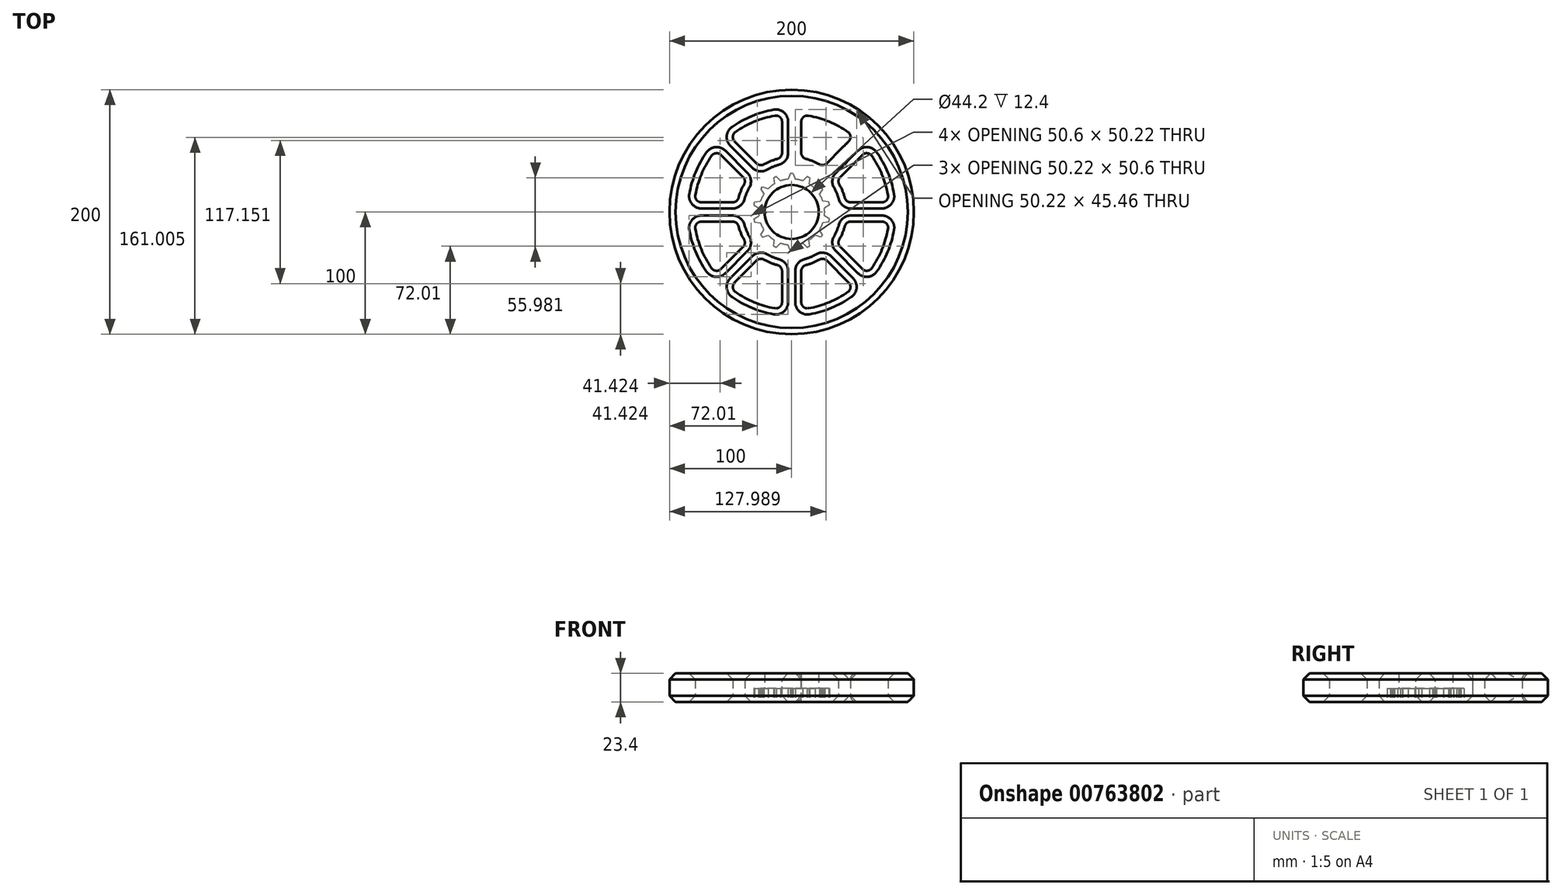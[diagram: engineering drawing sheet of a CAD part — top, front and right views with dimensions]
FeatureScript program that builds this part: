
annotation { "Feature Type Name" : "Feature", "Feature Type Description" : "" }
export const myFeature = defineFeature(function(context is Context, id is Id, definition is map)
    precondition{}
    {
        {
            var Q0;
            Q0=qCreatedBy(makeId("Top.planeOp"),FACE);
            var sketch = newSketch(context, id + "F0", { "sketchPlane" : qUnion([Q0])});
            skCircle(sketch, "E0", {"center": v(0, 0) * mm, "radius": 22.1 * mm});
            skCircle(sketch, "E1", {"center": v(0, 0) * mm, "radius": 100 * mm});
            skSolve(sketch);
        }
        {
            var Q0;
            Q0 = qSketchRegion(id + "F0", true);
            extrude(context, id + "F1", {"entities" : qUnion([Q0]), "depth" : 23.4 * mm, "offsetDistance" : 25 * mm});
        }
        {
            var Q0;
            Q0=makeQuery(id+"F1.opExtrude","CAP_FACE",FACE,{"disambiguationData":[OSD([sQuery(id+"F0.wireOp",EDGE,"E0"),sQuery(id+"F0.wireOp",EDGE,"E1")])],"isStart":true});
            var sketch = newSketch(context, id + "F2", { "sketchPlane" : qUnion([Q0])});
            skCircle(sketch, "E2.0", {"center": v(0, 0) * mm, "radius": 22.1 * mm});
            skArc(sketch, "E3", {"start": v(2.9, -26.84) * mm, "mid": v(6, -26.32) * mm, "end": v(9.03, -25.44) * mm});
            skLineSegment(sketch, "E4", {"start": v(0, 0) * mm, "end": v(0, 59.3) * mm, "construction": true});
            skArc(sketch, "E5", {"start": v(0, -31.5) * mm, "mid": v(0.63, -31.5) * mm, "end": v(1.25, -31.48) * mm, "construction": true});
            skLineSegment(sketch, "E6", {"start": v(0, 31.5) * mm, "end": v(-1.25, 31.48) * mm});
            skLineSegment(sketch, "E7.MirrorCS", {"start": v(0, 31.5) * mm, "end": v(1.25, 31.48) * mm});
            skLineSegment(sketch, "E8", {"start": v(-1.25, 31.48) * mm, "end": v(-2.9, 26.84) * mm});
            skLineSegment(sketch, "E9", {"start": v(1.25, 31.48) * mm, "end": v(2.9, 26.84) * mm});
            skArc(sketch, "E10.1.0", {"start": v(0, -31.5) * mm, "mid": v(0.63, -31.5) * mm, "end": v(1.25, -31.48) * mm});
            skLineSegment(sketch, "E11.1.0", {"start": v(-12.53, 28.9) * mm, "end": v(-9.03, 25.44) * mm});
            skLineSegment(sketch, "E11.1.1", {"start": v(-14.78, 27.82) * mm, "end": v(-14.26, 22.93) * mm});
            skLineSegment(sketch, "E11.1.2", {"start": v(-13.67, 28.38) * mm, "end": v(-12.53, 28.9) * mm});
            skLineSegment(sketch, "E11.1.3", {"start": v(-13.67, 28.38) * mm, "end": v(-14.78, 27.82) * mm});
            skLineSegment(sketch, "E11.2.0", {"start": v(-23.83, 20.6) * mm, "end": v(-19.18, 19) * mm});
            skLineSegment(sketch, "E11.2.1", {"start": v(-25.39, 18.65) * mm, "end": v(-22.8, 14.47) * mm});
            skLineSegment(sketch, "E11.2.2", {"start": v(-24.63, 19.64) * mm, "end": v(-23.83, 20.6) * mm});
            skLineSegment(sketch, "E11.2.3", {"start": v(-24.63, 19.64) * mm, "end": v(-25.39, 18.65) * mm});
            skLineSegment(sketch, "E11.3.0", {"start": v(-30.4, 8.22) * mm, "end": v(-25.53, 8.8) * mm});
            skLineSegment(sketch, "E11.3.1", {"start": v(-30.96, 5.79) * mm, "end": v(-26.82, 3.15) * mm});
            skLineSegment(sketch, "E11.3.2", {"start": v(-30.71, 7) * mm, "end": v(-30.4, 8.22) * mm});
            skLineSegment(sketch, "E11.3.3", {"start": v(-30.71, 7) * mm, "end": v(-30.96, 5.79) * mm});
            skLineSegment(sketch, "E11.4.0", {"start": v(-30.96, -5.79) * mm, "end": v(-26.82, -3.15) * mm});
            skLineSegment(sketch, "E11.4.1", {"start": v(-30.4, -8.22) * mm, "end": v(-25.53, -8.8) * mm});
            skLineSegment(sketch, "E11.4.2", {"start": v(-30.71, -7) * mm, "end": v(-30.96, -5.79) * mm});
            skLineSegment(sketch, "E11.4.3", {"start": v(-30.71, -7) * mm, "end": v(-30.4, -8.22) * mm});
            skLineSegment(sketch, "E11.5.0", {"start": v(-25.39, -18.65) * mm, "end": v(-22.8, -14.47) * mm});
            skLineSegment(sketch, "E11.5.1", {"start": v(-23.83, -20.6) * mm, "end": v(-19.18, -19) * mm});
            skLineSegment(sketch, "E11.5.2", {"start": v(-24.63, -19.64) * mm, "end": v(-25.39, -18.65) * mm});
            skLineSegment(sketch, "E11.5.3", {"start": v(-24.63, -19.64) * mm, "end": v(-23.83, -20.6) * mm});
            skLineSegment(sketch, "E11.6.0", {"start": v(-14.78, -27.82) * mm, "end": v(-14.26, -22.93) * mm});
            skLineSegment(sketch, "E11.6.1", {"start": v(-12.53, -28.9) * mm, "end": v(-9.03, -25.44) * mm});
            skLineSegment(sketch, "E11.6.2", {"start": v(-13.67, -28.38) * mm, "end": v(-14.78, -27.82) * mm});
            skLineSegment(sketch, "E11.6.3", {"start": v(-13.67, -28.38) * mm, "end": v(-12.53, -28.9) * mm});
            skLineSegment(sketch, "E11.7.0", {"start": v(-1.25, -31.48) * mm, "end": v(-2.9, -26.84) * mm});
            skLineSegment(sketch, "E11.7.1", {"start": v(1.25, -31.48) * mm, "end": v(2.9, -26.84) * mm});
            skLineSegment(sketch, "E11.7.2", {"start": v(0, -31.5) * mm, "end": v(-1.25, -31.48) * mm});
            skLineSegment(sketch, "E11.7.3", {"start": v(0, -31.5) * mm, "end": v(1.25, -31.48) * mm});
            skLineSegment(sketch, "E11.8.0", {"start": v(12.53, -28.9) * mm, "end": v(9.03, -25.44) * mm});
            skLineSegment(sketch, "E11.8.1", {"start": v(14.78, -27.82) * mm, "end": v(14.26, -22.93) * mm});
            skLineSegment(sketch, "E11.8.2", {"start": v(13.67, -28.38) * mm, "end": v(12.53, -28.9) * mm});
            skLineSegment(sketch, "E11.8.3", {"start": v(13.67, -28.38) * mm, "end": v(14.78, -27.82) * mm});
            skLineSegment(sketch, "E11.9.0", {"start": v(23.83, -20.6) * mm, "end": v(19.18, -19) * mm});
            skLineSegment(sketch, "E11.9.1", {"start": v(25.39, -18.65) * mm, "end": v(22.8, -14.47) * mm});
            skLineSegment(sketch, "E11.9.2", {"start": v(24.63, -19.64) * mm, "end": v(23.83, -20.6) * mm});
            skLineSegment(sketch, "E11.9.3", {"start": v(24.63, -19.64) * mm, "end": v(25.39, -18.65) * mm});
            skLineSegment(sketch, "E11.10.0", {"start": v(30.4, -8.22) * mm, "end": v(25.53, -8.8) * mm});
            skLineSegment(sketch, "E11.10.1", {"start": v(30.96, -5.79) * mm, "end": v(26.82, -3.15) * mm});
            skLineSegment(sketch, "E11.10.2", {"start": v(30.71, -7) * mm, "end": v(30.4, -8.22) * mm});
            skLineSegment(sketch, "E11.10.3", {"start": v(30.71, -7) * mm, "end": v(30.96, -5.79) * mm});
            skLineSegment(sketch, "E11.11.0", {"start": v(30.96, 5.79) * mm, "end": v(26.82, 3.15) * mm});
            skLineSegment(sketch, "E11.11.1", {"start": v(30.4, 8.22) * mm, "end": v(25.53, 8.8) * mm});
            skLineSegment(sketch, "E11.11.2", {"start": v(30.71, 7) * mm, "end": v(30.96, 5.79) * mm});
            skLineSegment(sketch, "E11.11.3", {"start": v(30.71, 7) * mm, "end": v(30.4, 8.22) * mm});
            skLineSegment(sketch, "E11.12.0", {"start": v(25.39, 18.65) * mm, "end": v(22.8, 14.47) * mm});
            skLineSegment(sketch, "E11.12.1", {"start": v(23.83, 20.6) * mm, "end": v(19.18, 19) * mm});
            skLineSegment(sketch, "E11.12.2", {"start": v(24.63, 19.64) * mm, "end": v(25.39, 18.65) * mm});
            skLineSegment(sketch, "E11.12.3", {"start": v(24.63, 19.64) * mm, "end": v(23.83, 20.6) * mm});
            skLineSegment(sketch, "E11.13.0", {"start": v(14.78, 27.82) * mm, "end": v(14.26, 22.93) * mm});
            skLineSegment(sketch, "E11.13.1", {"start": v(12.53, 28.9) * mm, "end": v(9.03, 25.44) * mm});
            skLineSegment(sketch, "E11.13.2", {"start": v(13.67, 28.38) * mm, "end": v(14.78, 27.82) * mm});
            skLineSegment(sketch, "E11.13.3", {"start": v(13.67, 28.38) * mm, "end": v(12.53, 28.9) * mm});
            skArc(sketch, "E12.trimOffspring", {"start": v(-2.9, 26.84) * mm, "mid": v(-6, 26.32) * mm, "end": v(-9.03, 25.44) * mm, "construction": true});
            skPoint(sketch, "E13.start.orphan", {"position": v(0, 27) * mm});
            skArc(sketch, "E14.trimOffspring", {"start": v(-2.9, 26.84) * mm, "mid": v(-6, 26.32) * mm, "end": v(-9.03, 25.44) * mm});
            skArc(sketch, "E15.trimOffspring", {"start": v(-12.53, 28.9) * mm, "mid": v(-13.67, 28.38) * mm, "end": v(-14.78, 27.82) * mm, "construction": true});
            skArc(sketch, "E16.trimOffspring", {"start": v(-12.53, 28.9) * mm, "mid": v(-13.67, 28.38) * mm, "end": v(-14.78, 27.82) * mm});
            skArc(sketch, "E17.trimOffspring", {"start": v(1.25, 31.48) * mm, "mid": v(0, 31.5) * mm, "end": v(-1.25, 31.48) * mm, "construction": true});
            skArc(sketch, "E18.trimOffspring", {"start": v(1.25, 31.48) * mm, "mid": v(0, 31.5) * mm, "end": v(-1.25, 31.48) * mm});
            skArc(sketch, "E19.trimOffspring", {"start": v(9.03, 25.44) * mm, "mid": v(6, 26.32) * mm, "end": v(2.9, 26.84) * mm});
            skArc(sketch, "E20.trimOffspring", {"start": v(14.78, 27.82) * mm, "mid": v(13.67, 28.38) * mm, "end": v(12.53, 28.9) * mm, "construction": true});
            skArc(sketch, "E21.trimOffspring", {"start": v(14.78, 27.82) * mm, "mid": v(13.67, 28.38) * mm, "end": v(12.53, 28.9) * mm});
            skArc(sketch, "E22.trimOffspring", {"start": v(25.39, 18.65) * mm, "mid": v(24.63, 19.64) * mm, "end": v(23.83, 20.6) * mm, "construction": true});
            skArc(sketch, "E23.trimOffspring", {"start": v(19.18, 19) * mm, "mid": v(16.83, 21.1) * mm, "end": v(14.26, 22.93) * mm});
            skArc(sketch, "E24.trimOffspring", {"start": v(25.39, 18.65) * mm, "mid": v(24.63, 19.64) * mm, "end": v(23.83, 20.6) * mm});
            skArc(sketch, "E25.trimOffspring", {"start": v(25.53, 8.8) * mm, "mid": v(24.33, 11.71) * mm, "end": v(22.8, 14.47) * mm});
            skArc(sketch, "E26.trimOffspring", {"start": v(30.96, 5.79) * mm, "mid": v(30.71, 7) * mm, "end": v(30.4, 8.22) * mm, "construction": true});
            skArc(sketch, "E27.trimOffspring", {"start": v(30.96, 5.79) * mm, "mid": v(30.71, 7) * mm, "end": v(30.4, 8.22) * mm});
            skArc(sketch, "E28.trimOffspring", {"start": v(30.4, -8.22) * mm, "mid": v(30.71, -7) * mm, "end": v(30.96, -5.79) * mm, "construction": true});
            skArc(sketch, "E29.trimOffspring", {"start": v(30.4, -8.22) * mm, "mid": v(30.71, -7) * mm, "end": v(30.96, -5.79) * mm});
            skArc(sketch, "E30.trimOffspring", {"start": v(26.82, -3.15) * mm, "mid": v(27, 0) * mm, "end": v(26.82, 3.15) * mm});
            skArc(sketch, "E31.trimOffspring", {"start": v(22.8, -14.47) * mm, "mid": v(24.33, -11.71) * mm, "end": v(25.53, -8.8) * mm});
            skArc(sketch, "E32.trimOffspring", {"start": v(23.83, -20.6) * mm, "mid": v(24.63, -19.64) * mm, "end": v(25.39, -18.65) * mm, "construction": true});
            skArc(sketch, "E33.trimOffspring", {"start": v(23.83, -20.6) * mm, "mid": v(24.63, -19.64) * mm, "end": v(25.39, -18.65) * mm});
            skArc(sketch, "E34.trimOffspring", {"start": v(14.26, -22.93) * mm, "mid": v(16.83, -21.1) * mm, "end": v(19.18, -19) * mm});
            skArc(sketch, "E35.trimOffspring", {"start": v(12.53, -28.9) * mm, "mid": v(13.67, -28.38) * mm, "end": v(14.78, -27.82) * mm, "construction": true});
            skArc(sketch, "E36.trimOffspring", {"start": v(12.53, -28.9) * mm, "mid": v(13.67, -28.38) * mm, "end": v(14.78, -27.82) * mm});
            skPoint(sketch, "E37.orphan", {"position": v(0, -27) * mm});
            skArc(sketch, "E38.trimOffspring", {"start": v(-1.25, -31.48) * mm, "mid": v(-1.07, -31.48) * mm, "end": v(-0.88, -31.49) * mm, "construction": true});
            skArc(sketch, "E39.trimOffspring", {"start": v(-1.25, -31.48) * mm, "mid": v(-1.07, -31.48) * mm, "end": v(-0.88, -31.49) * mm});
            skArc(sketch, "E40.trimOffspring", {"start": v(-9.03, -25.44) * mm, "mid": v(-6, -26.32) * mm, "end": v(-2.9, -26.84) * mm, "construction": true});
            skArc(sketch, "E41.trimOffspring", {"start": v(-9.03, -25.44) * mm, "mid": v(-6, -26.32) * mm, "end": v(-2.9, -26.84) * mm});
            skArc(sketch, "E42.trimOffspring", {"start": v(-14.78, -27.82) * mm, "mid": v(-13.67, -28.38) * mm, "end": v(-12.53, -28.9) * mm, "construction": true});
            skArc(sketch, "E43.trimOffspring", {"start": v(-14.78, -27.82) * mm, "mid": v(-13.67, -28.38) * mm, "end": v(-12.53, -28.9) * mm});
            skArc(sketch, "E44.trimOffspring", {"start": v(-25.39, -18.65) * mm, "mid": v(-24.63, -19.64) * mm, "end": v(-23.83, -20.6) * mm, "construction": true});
            skArc(sketch, "E45.trimOffspring", {"start": v(-25.39, -18.65) * mm, "mid": v(-25.01, -19.15) * mm, "end": v(-24.63, -19.64) * mm});
            skArc(sketch, "E46.trimOffspring", {"start": v(-30.96, -5.79) * mm, "mid": v(-30.84, -6.4) * mm, "end": v(-30.71, -7) * mm, "construction": true});
            skArc(sketch, "E47.trimOffspring", {"start": v(-30.96, -5.79) * mm, "mid": v(-30.84, -6.4) * mm, "end": v(-30.71, -7) * mm});
            skArc(sketch, "E48.trimOffspring", {"start": v(-30.4, 8.22) * mm, "mid": v(-30.71, 7) * mm, "end": v(-30.96, 5.79) * mm, "construction": true});
            skArc(sketch, "E49.trimOffspring", {"start": v(-30.4, 8.22) * mm, "mid": v(-30.71, 7) * mm, "end": v(-30.96, 5.79) * mm});
            skArc(sketch, "E50.trimOffspring", {"start": v(-23.83, 20.6) * mm, "mid": v(-24.63, 19.64) * mm, "end": v(-25.39, 18.65) * mm, "construction": true});
            skArc(sketch, "E51.trimOffspring", {"start": v(-23.83, 20.6) * mm, "mid": v(-24.63, 19.64) * mm, "end": v(-25.39, 18.65) * mm});
            skArc(sketch, "E52.trimOffspring", {"start": v(-19.18, -19) * mm, "mid": v(-16.83, -21.1) * mm, "end": v(-14.26, -22.93) * mm});
            skArc(sketch, "E53.trimOffspring", {"start": v(-25.53, -8.8) * mm, "mid": v(-24.33, -11.71) * mm, "end": v(-22.8, -14.47) * mm});
            skArc(sketch, "E54.trimOffspring", {"start": v(-26.82, 3.15) * mm, "mid": v(-27, 0) * mm, "end": v(-26.82, -3.15) * mm});
            skArc(sketch, "E55.trimOffspring", {"start": v(-22.8, 14.47) * mm, "mid": v(-24.33, 11.71) * mm, "end": v(-25.53, 8.8) * mm, "construction": true});
            skArc(sketch, "E56.trimOffspring", {"start": v(-22.8, 14.47) * mm, "mid": v(-24.33, 11.71) * mm, "end": v(-25.53, 8.8) * mm});
            skArc(sketch, "E57.trimOffspring", {"start": v(-14.26, 22.93) * mm, "mid": v(-16.83, 21.1) * mm, "end": v(-19.18, 19) * mm, "construction": true});
            skArc(sketch, "E58.trimOffspring", {"start": v(-14.26, 22.93) * mm, "mid": v(-16.83, 21.1) * mm, "end": v(-19.18, 19) * mm});
            skSolve(sketch);
        }
        {
            var Q0;
            Q0 = qSketchRegion(id + "F2", true);
            extrude(context, id + "F3", {"entities" : qUnion([Q0]), "operationType" : NewBodyOperationType.REMOVE, "oppositeDirection" : true, "depth" : 11 * mm, "offsetDistance" : 25 * mm});
        }
        {
            var Q0;
            Q0=makeQuery(id+"F1.opExtrude","CAP_FACE",FACE,{"disambiguationData":[OSD([sQuery(id+"F0.wireOp",EDGE,"E0"),sQuery(id+"F0.wireOp",EDGE,"E1")])],"isStart":true});
            var sketch = newSketch(context, id + "F4", { "sketchPlane" : qUnion([Q0])});
            skArc(sketch, "E59", {"start": v(-36.9, 25.76) * mm, "mid": v(-41.57, 17.22) * mm, "end": v(-44.3, 7.88) * mm});
            skArc(sketch, "E60", {"start": v(-61.87, 50.72) * mm, "mid": v(-73.91, 30.61) * mm, "end": v(-79.61, 7.88) * mm});
            skLineSegment(sketch, "E61", {"start": v(0, 0) * mm, "end": v(0, 117.13) * mm, "construction": true});
            skLineSegment(sketch, "E62", {"start": v(-7.88, 79.61) * mm, "end": v(-7.88, 44.3) * mm});
            skLineSegment(sketch, "E63.MirrorCS", {"start": v(7.88, 79.61) * mm, "end": v(7.88, 44.3) * mm});
            skLineSegment(sketch, "E64.1.0", {"start": v(-61.87, 50.72) * mm, "end": v(-36.9, 25.76) * mm});
            skLineSegment(sketch, "E64.1.1", {"start": v(-50.72, 61.87) * mm, "end": v(-25.76, 36.9) * mm});
            skLineSegment(sketch, "E64.2.0", {"start": v(-79.61, -7.88) * mm, "end": v(-44.3, -7.88) * mm});
            skLineSegment(sketch, "E64.2.1", {"start": v(-79.61, 7.88) * mm, "end": v(-44.3, 7.88) * mm});
            skLineSegment(sketch, "E64.3.0", {"start": v(-50.72, -61.87) * mm, "end": v(-25.76, -36.9) * mm});
            skLineSegment(sketch, "E64.3.1", {"start": v(-61.87, -50.72) * mm, "end": v(-36.9, -25.76) * mm});
            skLineSegment(sketch, "E64.4.0", {"start": v(7.88, -79.61) * mm, "end": v(7.88, -44.3) * mm});
            skLineSegment(sketch, "E64.4.1", {"start": v(-7.88, -79.61) * mm, "end": v(-7.88, -44.3) * mm});
            skLineSegment(sketch, "E64.5.0", {"start": v(61.87, -50.72) * mm, "end": v(36.9, -25.76) * mm});
            skLineSegment(sketch, "E64.5.1", {"start": v(50.72, -61.87) * mm, "end": v(25.76, -36.9) * mm});
            skLineSegment(sketch, "E64.6.0", {"start": v(79.61, 7.88) * mm, "end": v(44.3, 7.88) * mm});
            skLineSegment(sketch, "E64.6.1", {"start": v(79.61, -7.88) * mm, "end": v(44.3, -7.88) * mm});
            skLineSegment(sketch, "E64.7.0", {"start": v(50.72, 61.87) * mm, "end": v(25.76, 36.9) * mm});
            skLineSegment(sketch, "E64.7.1", {"start": v(61.87, 50.72) * mm, "end": v(36.9, 25.76) * mm});
            skArc(sketch, "E65.trimOffspring", {"start": v(-7.88, 44.3) * mm, "mid": v(-17.22, 41.57) * mm, "end": v(-25.76, 36.9) * mm});
            skArc(sketch, "E66.trimOffspring", {"start": v(-7.88, 79.61) * mm, "mid": v(-30.61, 73.91) * mm, "end": v(-50.72, 61.87) * mm});
            skArc(sketch, "E67.trimOffspring", {"start": v(50.72, 61.87) * mm, "mid": v(30.61, 73.91) * mm, "end": v(7.88, 79.61) * mm});
            skArc(sketch, "E68.trimOffspring", {"start": v(25.76, 36.9) * mm, "mid": v(17.22, 41.57) * mm, "end": v(7.88, 44.3) * mm});
            skArc(sketch, "E69.trimOffspring", {"start": v(44.3, 7.88) * mm, "mid": v(41.57, 17.22) * mm, "end": v(36.9, 25.76) * mm});
            skArc(sketch, "E70.trimOffspring", {"start": v(79.61, 7.88) * mm, "mid": v(73.91, 30.61) * mm, "end": v(61.87, 50.72) * mm});
            skArc(sketch, "E71.trimOffspring", {"start": v(61.87, -50.72) * mm, "mid": v(73.91, -30.61) * mm, "end": v(79.61, -7.88) * mm});
            skArc(sketch, "E72.trimOffspring", {"start": v(36.9, -25.76) * mm, "mid": v(41.57, -17.22) * mm, "end": v(44.3, -7.88) * mm});
            skArc(sketch, "E73.trimOffspring", {"start": v(7.88, -44.3) * mm, "mid": v(17.22, -41.57) * mm, "end": v(25.76, -36.9) * mm});
            skArc(sketch, "E74.trimOffspring", {"start": v(7.88, -79.61) * mm, "mid": v(30.61, -73.91) * mm, "end": v(50.72, -61.87) * mm});
            skArc(sketch, "E75.trimOffspring", {"start": v(-50.72, -61.87) * mm, "mid": v(-30.61, -73.91) * mm, "end": v(-7.88, -79.61) * mm});
            skArc(sketch, "E76.trimOffspring", {"start": v(-25.76, -36.9) * mm, "mid": v(-17.22, -41.57) * mm, "end": v(-7.88, -44.3) * mm});
            skArc(sketch, "E77.trimOffspring", {"start": v(-79.61, -7.88) * mm, "mid": v(-73.91, -30.61) * mm, "end": v(-61.87, -50.72) * mm});
            skArc(sketch, "E78.trimOffspring", {"start": v(-44.3, -7.88) * mm, "mid": v(-41.57, -17.22) * mm, "end": v(-36.9, -25.76) * mm});
            skSolve(sketch);
        }
        {
            var Q0;
            Q0=makeQuery(id+"F4.imprint","IMPRINT",FACE,{"disambiguationData":[TD([[makeQuery(id+"F4.imprint","IMPRINT",EDGE,{"derivedFrom":sQuery(id+"F4.wireOp",EDGE,"E59")}),-1.0]])]});
            var Q1;
            Q1=makeQuery(id+"F4.imprint","IMPRINT",FACE,{"disambiguationData":[TD([[makeQuery(id+"F4.imprint","IMPRINT",EDGE,{"derivedFrom":sQuery(id+"F4.wireOp",EDGE,"E62")}),-1.0]])]});
            var Q2;
            Q2=makeQuery(id+"F4.imprint","IMPRINT",FACE,{"disambiguationData":[TD([[makeQuery(id+"F4.imprint","IMPRINT",EDGE,{"derivedFrom":sQuery(id+"F4.wireOp",EDGE,"E63.MirrorCS")}),1.0]])]});
            var Q3;
            Q3=makeQuery(id+"F4.imprint","IMPRINT",FACE,{"disambiguationData":[TD([[makeQuery(id+"F4.imprint","IMPRINT",EDGE,{"derivedFrom":sQuery(id+"F4.wireOp",EDGE,"E64.6.0")}),-1.0]])]});
            var Q4;
            Q4=makeQuery(id+"F4.imprint","IMPRINT",FACE,{"disambiguationData":[TD([[makeQuery(id+"F4.imprint","IMPRINT",EDGE,{"derivedFrom":sQuery(id+"F4.wireOp",EDGE,"E64.5.0")}),-1.0]])]});
            var Q5;
            Q5=makeQuery(id+"F4.imprint","IMPRINT",FACE,{"disambiguationData":[TD([[makeQuery(id+"F4.imprint","IMPRINT",EDGE,{"derivedFrom":sQuery(id+"F4.wireOp",EDGE,"E64.4.0")}),-1.0]])]});
            var Q6;
            Q6=makeQuery(id+"F4.imprint","IMPRINT",FACE,{"disambiguationData":[TD([[makeQuery(id+"F4.imprint","IMPRINT",EDGE,{"derivedFrom":sQuery(id+"F4.wireOp",EDGE,"E64.3.0")}),-1.0]])]});
            var Q7;
            Q7=makeQuery(id+"F4.imprint","IMPRINT",FACE,{"disambiguationData":[TD([[makeQuery(id+"F4.imprint","IMPRINT",EDGE,{"derivedFrom":sQuery(id+"F4.wireOp",EDGE,"E64.2.0")}),-1.0]])]});
            extrude(context, id + "F5", {"entities" : qUnion([Q0, Q1, Q2, Q3, Q4, Q5, Q6, Q7]), "operationType" : NewBodyOperationType.REMOVE, "oppositeDirection" : true, "depth" : 25 * mm, "offsetDistance" : 25 * mm});
        }
        {
            var Q0;
            Q0=makeQuery(id+"F5.boolean.opBoolean","COPY",EDGE,{"derivedFrom":makeQuery(id+"F5.opExtrude","SWEPT_EDGE",EDGE,{"disambiguationData":[OSD([sQuery(id+"F4.wireOp",EDGE,"E60"),sQuery(id+"F4.wireOp",EDGE,"E64.1.0")])]})});
            var Q1;
            Q1=makeQuery(id+"F5.boolean.opBoolean","COPY",EDGE,{"derivedFrom":makeQuery(id+"F5.opExtrude","SWEPT_EDGE",EDGE,{"disambiguationData":[OSD([sQuery(id+"F4.wireOp",EDGE,"E64.1.1"),sQuery(id+"F4.wireOp",EDGE,"E66.trimOffspring")])]})});
            var Q2;
            Q2=makeQuery(id+"F5.boolean.opBoolean","COPY",EDGE,{"derivedFrom":makeQuery(id+"F5.opExtrude","SWEPT_EDGE",EDGE,{"disambiguationData":[OSD([sQuery(id+"F4.wireOp",EDGE,"E59"),sQuery(id+"F4.wireOp",EDGE,"E64.1.0")])]})});
            var Q3;
            Q3=makeQuery(id+"F5.boolean.opBoolean","COPY",EDGE,{"derivedFrom":makeQuery(id+"F5.opExtrude","SWEPT_EDGE",EDGE,{"disambiguationData":[OSD([sQuery(id+"F4.wireOp",EDGE,"E62"),sQuery(id+"F4.wireOp",EDGE,"E65.trimOffspring")])]})});
            var Q4;
            Q4=makeQuery(id+"F5.boolean.opBoolean","COPY",EDGE,{"derivedFrom":makeQuery(id+"F5.opExtrude","SWEPT_EDGE",EDGE,{"disambiguationData":[OSD([sQuery(id+"F4.wireOp",EDGE,"E59"),sQuery(id+"F4.wireOp",EDGE,"E64.2.1")])]})});
            var Q5;
            Q5=makeQuery(id+"F5.boolean.opBoolean","COPY",EDGE,{"derivedFrom":makeQuery(id+"F5.opExtrude","SWEPT_EDGE",EDGE,{"disambiguationData":[OSD([sQuery(id+"F4.wireOp",EDGE,"E64.7.0"),sQuery(id+"F4.wireOp",EDGE,"E68.trimOffspring")])]})});
            var Q6;
            Q6=makeQuery(id+"F5.boolean.opBoolean","COPY",EDGE,{"derivedFrom":makeQuery(id+"F5.opExtrude","SWEPT_EDGE",EDGE,{"disambiguationData":[OSD([sQuery(id+"F4.wireOp",EDGE,"E64.5.1"),sQuery(id+"F4.wireOp",EDGE,"E74.trimOffspring")])]})});
            var Q7;
            Q7=makeQuery(id+"F5.boolean.opBoolean","COPY",EDGE,{"derivedFrom":makeQuery(id+"F5.opExtrude","SWEPT_EDGE",EDGE,{"disambiguationData":[OSD([sQuery(id+"F4.wireOp",EDGE,"E64.3.1"),sQuery(id+"F4.wireOp",EDGE,"E78.trimOffspring")])]})});
            var Q8;
            Q8=makeQuery(id+"F5.boolean.opBoolean","COPY",EDGE,{"derivedFrom":makeQuery(id+"F5.opExtrude","SWEPT_EDGE",EDGE,{"disambiguationData":[OSD([sQuery(id+"F4.wireOp",EDGE,"E64.4.1"),sQuery(id+"F4.wireOp",EDGE,"E76.trimOffspring")])]})});
            var Q9;
            Q9=makeQuery(id+"F5.boolean.opBoolean","COPY",EDGE,{"derivedFrom":makeQuery(id+"F5.opExtrude","SWEPT_EDGE",EDGE,{"disambiguationData":[OSD([sQuery(id+"F4.wireOp",EDGE,"E64.2.0"),sQuery(id+"F4.wireOp",EDGE,"E78.trimOffspring")])]})});
            var Q10;
            Q10=makeQuery(id+"F5.boolean.opBoolean","COPY",EDGE,{"derivedFrom":makeQuery(id+"F5.opExtrude","SWEPT_EDGE",EDGE,{"disambiguationData":[OSD([sQuery(id+"F4.wireOp",EDGE,"E64.3.0"),sQuery(id+"F4.wireOp",EDGE,"E76.trimOffspring")])]})});
            var Q11;
            Q11=makeQuery(id+"F5.boolean.opBoolean","COPY",EDGE,{"derivedFrom":makeQuery(id+"F5.opExtrude","SWEPT_EDGE",EDGE,{"disambiguationData":[OSD([sQuery(id+"F4.wireOp",EDGE,"E64.4.0"),sQuery(id+"F4.wireOp",EDGE,"E73.trimOffspring")])]})});
            var Q12;
            Q12=makeQuery(id+"F5.boolean.opBoolean","COPY",EDGE,{"derivedFrom":makeQuery(id+"F5.opExtrude","SWEPT_EDGE",EDGE,{"disambiguationData":[OSD([sQuery(id+"F4.wireOp",EDGE,"E64.5.1"),sQuery(id+"F4.wireOp",EDGE,"E73.trimOffspring")])]})});
            var Q13;
            Q13=makeQuery(id+"F5.boolean.opBoolean","COPY",EDGE,{"derivedFrom":makeQuery(id+"F5.opExtrude","SWEPT_EDGE",EDGE,{"disambiguationData":[OSD([sQuery(id+"F4.wireOp",EDGE,"E64.5.0"),sQuery(id+"F4.wireOp",EDGE,"E72.trimOffspring")])]})});
            var Q14;
            Q14=makeQuery(id+"F5.boolean.opBoolean","COPY",EDGE,{"derivedFrom":makeQuery(id+"F5.opExtrude","SWEPT_EDGE",EDGE,{"disambiguationData":[OSD([sQuery(id+"F4.wireOp",EDGE,"E64.6.1"),sQuery(id+"F4.wireOp",EDGE,"E72.trimOffspring")])]})});
            var Q15;
            Q15=makeQuery(id+"F5.boolean.opBoolean","COPY",EDGE,{"derivedFrom":makeQuery(id+"F5.opExtrude","SWEPT_EDGE",EDGE,{"disambiguationData":[OSD([sQuery(id+"F4.wireOp",EDGE,"E64.6.0"),sQuery(id+"F4.wireOp",EDGE,"E69.trimOffspring")])]})});
            var Q16;
            Q16=makeQuery(id+"F5.boolean.opBoolean","COPY",EDGE,{"derivedFrom":makeQuery(id+"F5.opExtrude","SWEPT_EDGE",EDGE,{"disambiguationData":[OSD([sQuery(id+"F4.wireOp",EDGE,"E64.7.1"),sQuery(id+"F4.wireOp",EDGE,"E69.trimOffspring")])]})});
            var Q17;
            Q17=makeQuery(id+"F5.boolean.opBoolean","COPY",EDGE,{"derivedFrom":makeQuery(id+"F5.opExtrude","SWEPT_EDGE",EDGE,{"disambiguationData":[OSD([sQuery(id+"F4.wireOp",EDGE,"E63.MirrorCS"),sQuery(id+"F4.wireOp",EDGE,"E68.trimOffspring")])]})});
            var Q18;
            Q18=makeQuery(id+"F5.boolean.opBoolean","COPY",EDGE,{"derivedFrom":makeQuery(id+"F5.opExtrude","SWEPT_EDGE",EDGE,{"disambiguationData":[OSD([sQuery(id+"F4.wireOp",EDGE,"E64.1.1"),sQuery(id+"F4.wireOp",EDGE,"E65.trimOffspring")])]})});
            var Q19;
            Q19=makeQuery(id+"F5.boolean.opBoolean","COPY",EDGE,{"derivedFrom":makeQuery(id+"F5.opExtrude","SWEPT_EDGE",EDGE,{"disambiguationData":[OSD([sQuery(id+"F4.wireOp",EDGE,"E64.5.0"),sQuery(id+"F4.wireOp",EDGE,"E71.trimOffspring")])]})});
            var Q20;
            Q20=makeQuery(id+"F5.boolean.opBoolean","COPY",FACE,{"derivedFrom":makeQuery(id+"F5.opExtrude","SWEPT_FACE",FACE,{"disambiguationData":[OSD([sQuery(id+"F4.wireOp",EDGE,"E74.trimOffspring")])]})});
            var Q21;
            Q21=makeQuery(id+"F5.boolean.opBoolean","COPY",EDGE,{"derivedFrom":makeQuery(id+"F5.opExtrude","SWEPT_EDGE",EDGE,{"disambiguationData":[OSD([sQuery(id+"F4.wireOp",EDGE,"E64.4.1"),sQuery(id+"F4.wireOp",EDGE,"E75.trimOffspring")])]})});
            var Q22;
            Q22=makeQuery(id+"F5.boolean.opBoolean","COPY",EDGE,{"derivedFrom":makeQuery(id+"F5.opExtrude","SWEPT_EDGE",EDGE,{"disambiguationData":[OSD([sQuery(id+"F4.wireOp",EDGE,"E64.3.0"),sQuery(id+"F4.wireOp",EDGE,"E75.trimOffspring")])]})});
            var Q23;
            Q23=makeQuery(id+"F5.boolean.opBoolean","COPY",EDGE,{"derivedFrom":makeQuery(id+"F5.opExtrude","SWEPT_EDGE",EDGE,{"disambiguationData":[OSD([sQuery(id+"F4.wireOp",EDGE,"E64.3.1"),sQuery(id+"F4.wireOp",EDGE,"E77.trimOffspring")])]})});
            var Q24;
            Q24=makeQuery(id+"F5.boolean.opBoolean","COPY",EDGE,{"derivedFrom":makeQuery(id+"F5.opExtrude","SWEPT_EDGE",EDGE,{"disambiguationData":[OSD([sQuery(id+"F4.wireOp",EDGE,"E64.2.0"),sQuery(id+"F4.wireOp",EDGE,"E77.trimOffspring")])]})});
            var Q25;
            Q25=makeQuery(id+"F5.boolean.opBoolean","COPY",EDGE,{"derivedFrom":makeQuery(id+"F5.opExtrude","SWEPT_EDGE",EDGE,{"disambiguationData":[OSD([sQuery(id+"F4.wireOp",EDGE,"E60"),sQuery(id+"F4.wireOp",EDGE,"E64.2.1")])]})});
            var Q26;
            Q26=makeQuery(id+"F5.boolean.opBoolean","COPY",EDGE,{"derivedFrom":makeQuery(id+"F5.opExtrude","SWEPT_EDGE",EDGE,{"disambiguationData":[OSD([sQuery(id+"F4.wireOp",EDGE,"E62"),sQuery(id+"F4.wireOp",EDGE,"E66.trimOffspring")])]})});
            var Q27;
            Q27=makeQuery(id+"F5.boolean.opBoolean","COPY",EDGE,{"derivedFrom":makeQuery(id+"F5.opExtrude","SWEPT_EDGE",EDGE,{"disambiguationData":[OSD([sQuery(id+"F4.wireOp",EDGE,"E63.MirrorCS"),sQuery(id+"F4.wireOp",EDGE,"E67.trimOffspring")])]})});
            var Q28;
            Q28=makeQuery(id+"F5.boolean.opBoolean","COPY",EDGE,{"derivedFrom":makeQuery(id+"F5.opExtrude","SWEPT_EDGE",EDGE,{"disambiguationData":[OSD([sQuery(id+"F4.wireOp",EDGE,"E64.7.0"),sQuery(id+"F4.wireOp",EDGE,"E67.trimOffspring")])]})});
            var Q29;
            Q29=makeQuery(id+"F5.boolean.opBoolean","COPY",EDGE,{"derivedFrom":makeQuery(id+"F5.opExtrude","SWEPT_EDGE",EDGE,{"disambiguationData":[OSD([sQuery(id+"F4.wireOp",EDGE,"E64.7.1"),sQuery(id+"F4.wireOp",EDGE,"E70.trimOffspring")])]})});
            var Q30;
            Q30=makeQuery(id+"F5.boolean.opBoolean","COPY",EDGE,{"derivedFrom":makeQuery(id+"F5.opExtrude","SWEPT_EDGE",EDGE,{"disambiguationData":[OSD([sQuery(id+"F4.wireOp",EDGE,"E64.6.0"),sQuery(id+"F4.wireOp",EDGE,"E70.trimOffspring")])]})});
            var Q31;
            Q31=makeQuery(id+"F5.boolean.opBoolean","COPY",EDGE,{"derivedFrom":makeQuery(id+"F5.opExtrude","SWEPT_EDGE",EDGE,{"disambiguationData":[OSD([sQuery(id+"F4.wireOp",EDGE,"E64.6.1"),sQuery(id+"F4.wireOp",EDGE,"E71.trimOffspring")])]})});
            fillet(context, id + "F6", {"entities" : qUnion([Q0, Q1, Q2, Q3, Q4, Q5, Q6, Q7, Q8, Q9, Q10, Q11, Q12, Q13, Q14, Q15, Q16, Q17, Q18, Q19, Q20, Q21, Q22, Q23, Q24, Q25, Q26, Q27, Q28, Q29, Q30, Q31]), "radius" : 5 * mm, "tangentPropagation" : true, "allowEdgeOverflow" : false});
        }
        {
            var Q0;
            Q0=makeQuery(id+"F1.opExtrude","CAP_EDGE",EDGE,{"disambiguationData":[OSD([sQuery(id+"F0.wireOp",EDGE,"E1")])],"isStart":false});
            var Q1;
            Q1=makeQuery(id+"F1.opExtrude","CAP_EDGE",EDGE,{"disambiguationData":[OSD([sQuery(id+"F0.wireOp",EDGE,"E1")])],"isStart":true});
            var Q2;
            Q2=makeQuery(id+"F5.boolean.opBoolean","COPY",EDGE,{"derivedFrom":makeQuery(id+"F5.opExtrude","CAP_EDGE",EDGE,{"disambiguationData":[OSD([sQuery(id+"F4.wireOp",EDGE,"E75.trimOffspring")])],"isStart":true})});
            var Q3;
            Q3=makeQuery(id+"F5.boolean.opBoolean","COPY",FACE,{"derivedFrom":makeQuery(id+"F5.opExtrude","SWEPT_FACE",FACE,{"disambiguationData":[OSD([sQuery(id+"F4.wireOp",EDGE,"E77.trimOffspring")])]})});
            var Q4;
            Q4=makeQuery(id+"F5.boolean.opBoolean","COPY",FACE,{"derivedFrom":makeQuery(id+"F5.opExtrude","SWEPT_FACE",FACE,{"disambiguationData":[OSD([sQuery(id+"F4.wireOp",EDGE,"E75.trimOffspring")])]})});
            var Q5;
            Q5=makeQuery(id+"F5.boolean.opBoolean","COPY",FACE,{"derivedFrom":makeQuery(id+"F5.opExtrude","SWEPT_FACE",FACE,{"disambiguationData":[OSD([sQuery(id+"F4.wireOp",EDGE,"E60")])]})});
            var Q6;
            Q6=makeQuery(id+"F5.boolean.opBoolean","COPY",FACE,{"derivedFrom":makeQuery(id+"F5.opExtrude","SWEPT_FACE",FACE,{"disambiguationData":[OSD([sQuery(id+"F4.wireOp",EDGE,"E66.trimOffspring")])]})});
            var Q7;
            Q7=makeQuery(id+"F5.boolean.opBoolean","COPY",FACE,{"derivedFrom":makeQuery(id+"F5.opExtrude","SWEPT_FACE",FACE,{"disambiguationData":[OSD([sQuery(id+"F4.wireOp",EDGE,"E67.trimOffspring")])]})});
            var Q8;
            Q8=makeQuery(id+"F5.boolean.opBoolean","COPY",FACE,{"derivedFrom":makeQuery(id+"F5.opExtrude","SWEPT_FACE",FACE,{"disambiguationData":[OSD([sQuery(id+"F4.wireOp",EDGE,"E64.7.1")])]})});
            var Q9;
            Q9=makeQuery(id+"F5.boolean.opBoolean","INTERSECT",EDGE,{"derivedFrom":[makeQuery(id+"F1.opExtrude","CAP_FACE",FACE,{"disambiguationData":[OSD([sQuery(id+"F0.wireOp",EDGE,"E0"),sQuery(id+"F0.wireOp",EDGE,"E1")])],"isStart":false}),makeQuery(id+"F5.opExtrude","SWEPT_FACE",FACE,{"disambiguationData":[OSD([sQuery(id+"F4.wireOp",EDGE,"E64.5.0")])]})]});
            var Q10;
            Q10=makeQuery(id+"F5.boolean.opBoolean","COPY",FACE,{"derivedFrom":makeQuery(id+"F5.opExtrude","SWEPT_FACE",FACE,{"disambiguationData":[OSD([sQuery(id+"F4.wireOp",EDGE,"E64.5.0")])]})});
            chamfer(context, id + "F7", {"entities" : qUnion([Q0, Q1, Q2, Q3, Q4, Q5, Q6, Q7, Q8, Q9, Q10]), "width" : 5 * mm, "tangentPropagation" : true});
        }
    });
